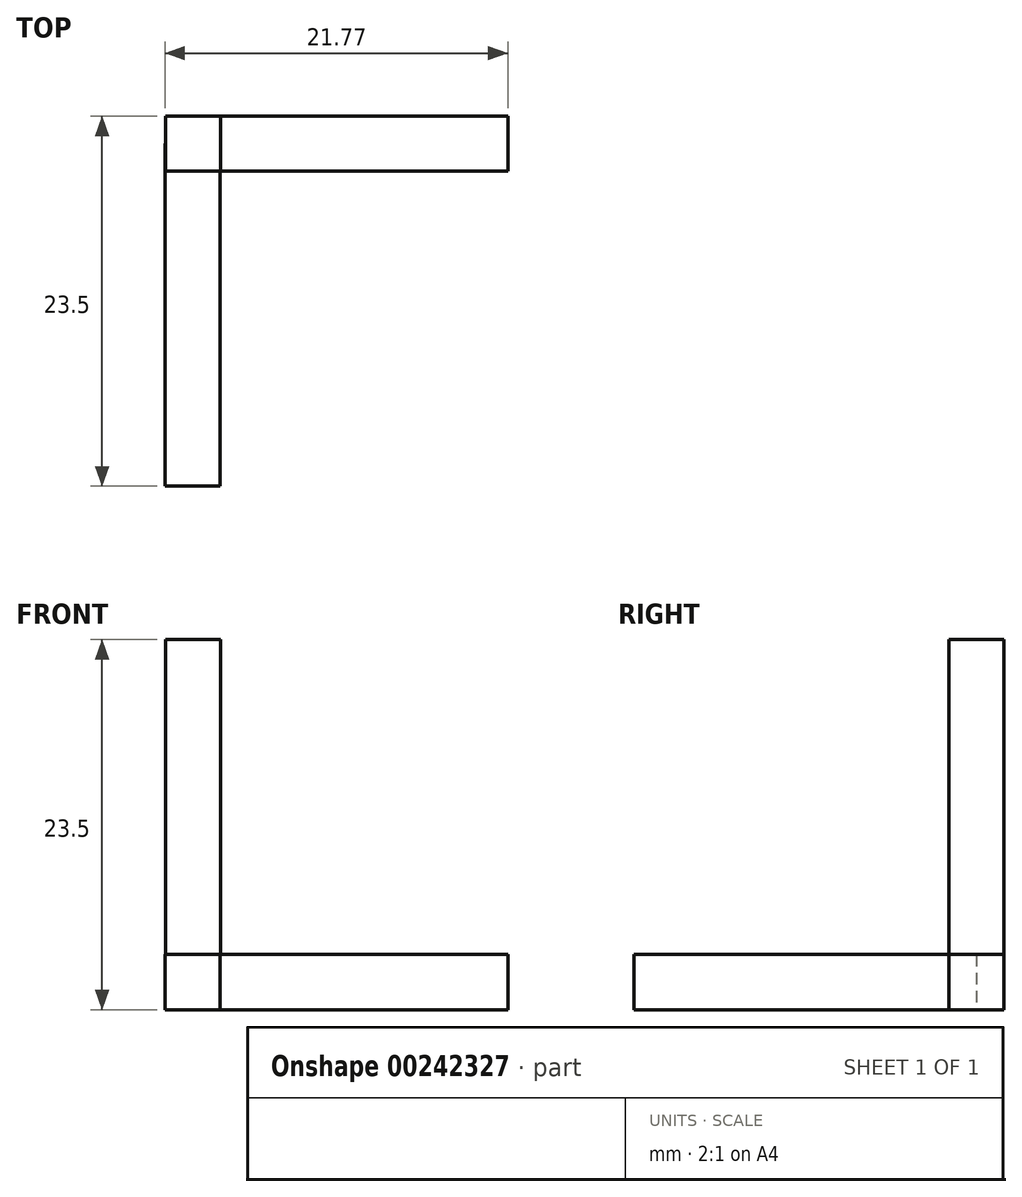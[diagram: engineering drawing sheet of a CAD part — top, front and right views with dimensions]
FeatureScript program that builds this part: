
annotation { "Feature Type Name" : "Feature", "Feature Type Description" : "" }
export const myFeature = defineFeature(function(context is Context, id is Id, definition is map)
    precondition{}
    {
        {
            var Q0;
            Q0=qCreatedBy(makeId("Top.planeOp"),FACE);
            var sketch = newSketch(context, id + "F0", { "sketchPlane" : qUnion([Q0])});
            skLineSegment(sketch, "E0.bottom", {"start": v(1.75, 1.75) * mm, "end": v(-1.75, 1.75) * mm});
            skLineSegment(sketch, "E0.top", {"start": v(1.75, -1.75) * mm, "end": v(-1.75, -1.75) * mm});
            skLineSegment(sketch, "E0.left", {"start": v(1.75, 1.75) * mm, "end": v(1.75, -1.75) * mm});
            skLineSegment(sketch, "E0.right", {"start": v(-1.75, 1.75) * mm, "end": v(-1.75, -1.75) * mm});
            skPoint(sketch, "E0.middle", {"position": v(0, 0) * mm});
            skSolve(sketch);
        }
        {
            var Q0;
            Q0 = qSketchRegion(id + "F0", true);
            extrude(context, id + "F1", {"entities" : qUnion([Q0]), "depth" : 23.5 * mm});
        }
        {
            var Q0;
            Q0=qCreatedBy(makeId("Right.planeOp"),FACE);
            var sketch = newSketch(context, id + "F2", { "sketchPlane" : qUnion([Q0])});
            skLineSegment(sketch, "E1.bottom", {"start": v(-1.75, 3.5) * mm, "end": v(1.75, 3.5) * mm});
            skLineSegment(sketch, "E1.left", {"start": v(-1.75, 3.5) * mm, "end": v(-1.75, 0) * mm});
            skLineSegment(sketch, "E1.right", {"start": v(1.75, 3.5) * mm, "end": v(1.75, 0) * mm});
            skPoint(sketch, "E1.middle", {"position": v(0, 0) * mm});
            skLineSegment(sketch, "E2", {"start": v(1.75, 0) * mm, "end": v(-1.75, 0) * mm});
            skSolve(sketch);
        }
        {
            var Q0;
            Q0 = qSketchRegion(id + "F2", true);
            extrude(context, id + "F3", {"entities" : qUnion([Q0]), "operationType" : NewBodyOperationType.ADD, "depth" : 20 * mm});
        }
        {
            var Q0;
            Q0=qCreatedBy(makeId("Front.planeOp"),FACE);
            var sketch = newSketch(context, id + "F4", { "sketchPlane" : qUnion([Q0])});
            skLineSegment(sketch, "E3", {"start": v(-81.46, 0) * mm, "end": v(-81.46, 1.5) * mm});
            skLineSegment(sketch, "E4.bottom", {"start": v(-1.77, 0) * mm, "end": v(1.73, 0) * mm});
            skLineSegment(sketch, "E4.top", {"start": v(-1.77, 3.5) * mm, "end": v(1.73, 3.5) * mm});
            skLineSegment(sketch, "E4.left", {"start": v(-1.77, 0) * mm, "end": v(-1.77, 3.5) * mm});
            skLineSegment(sketch, "E4.right", {"start": v(1.73, 0) * mm, "end": v(1.73, 3.5) * mm});
            skSolve(sketch);
        }
        {
            var Q0;
            Q0 = qSketchRegion(id + "F4", true);
            extrude(context, id + "F5", {"entities" : qUnion([Q0]), "operationType" : NewBodyOperationType.ADD, "depth" : 21.75 * mm});
        }
        {
            var Q0;
            Q0=makeQuery(id+"F1.opExtrude","SWEPT_BODY",BODY,{"disambiguationData":[OSD([sQuery(id+"F0.wireOp",EDGE,"E0.bottom"),sQuery(id+"F0.wireOp",EDGE,"E0.top"),sQuery(id+"F0.wireOp",EDGE,"E0.left"),sQuery(id+"F0.wireOp",EDGE,"E0.right")])]});
            transform(context, id + "F6", {"entities" : qUnion([Q0]), "transformType" : TransformType.TRANSLATION_3D, "dx" : 0 * mm, "dy" : 0 * mm, "dz" : 0 * mm, "makeCopy" : true});
        }
    });
